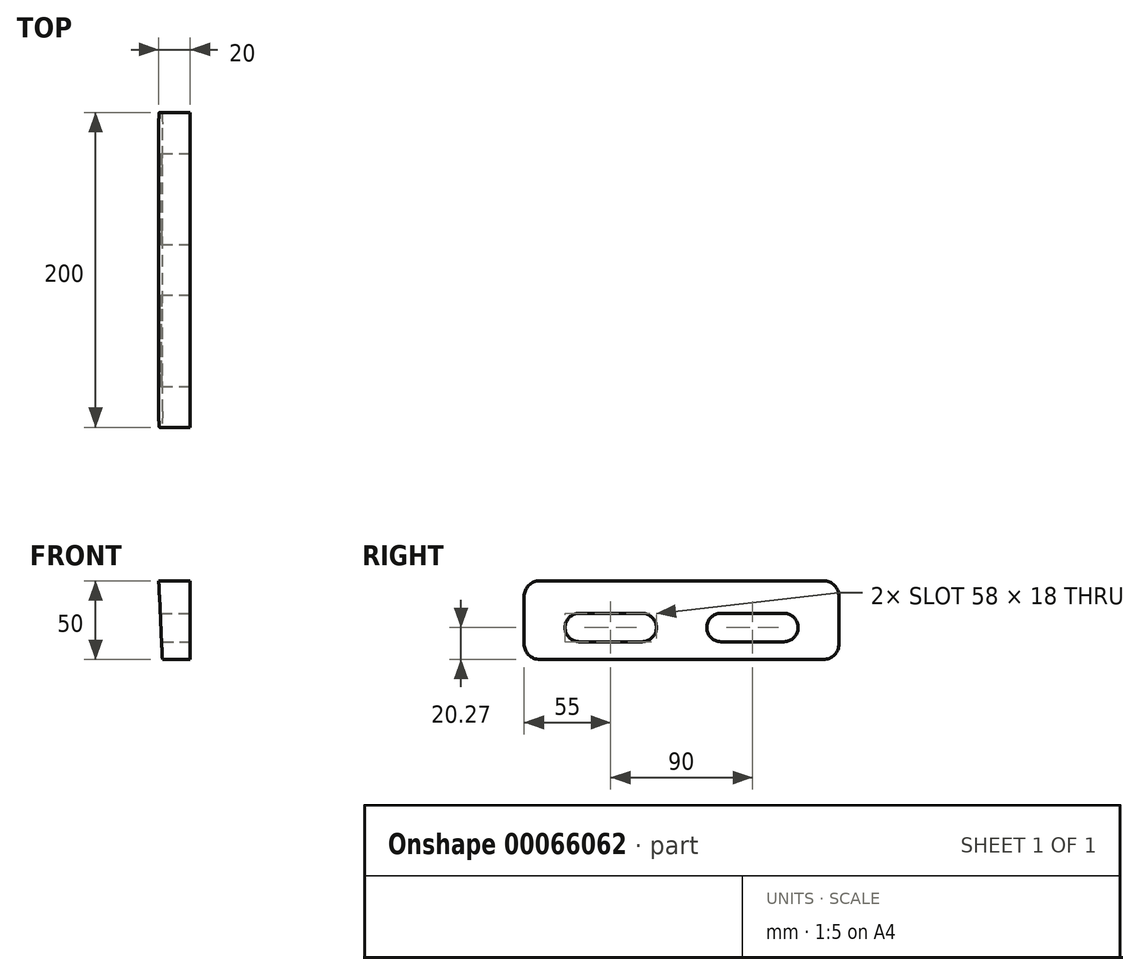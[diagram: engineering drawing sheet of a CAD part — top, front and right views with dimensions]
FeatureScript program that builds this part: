
annotation { "Feature Type Name" : "Feature", "Feature Type Description" : "" }
export const myFeature = defineFeature(function(context is Context, id is Id, definition is map)
    precondition{}
    {
        {
            var Q0;
            Q0=qCreatedBy(makeId("Front.planeOp"),FACE);
            var sketch = newSketch(context, id + "F0", { "sketchPlane" : qUnion([Q0])});
            skLineSegment(sketch, "E0", {"start": v(6.85, 29.73) * mm, "end": v(6.85, -20.27) * mm});
            skLineSegment(sketch, "E1", {"start": v(6.85, -20.27) * mm, "end": v(-10.8, -20.27) * mm});
            skLineSegment(sketch, "E2", {"start": v(-10.8, -20.27) * mm, "end": v(-13.15, 29.73) * mm});
            skLineSegment(sketch, "E3", {"start": v(-13.15, 29.73) * mm, "end": v(6.85, 29.73) * mm});
            skLineSegment(sketch, "E4", {"start": v(-13.15, 29.73) * mm, "end": v(-13.15, -60.05) * mm, "construction": true});
            skSolve(sketch);
        }
        {
            var Q0;
            Q0=makeQuery(id+"F0.imprint","IMPRINT",FACE,{"disambiguationData":[TD([[makeQuery(id+"F0.imprint","IMPRINT",EDGE,{"derivedFrom":sQuery(id+"F0.wireOp",EDGE,"E0")}),-1.0]])]});
            extrude(context, id + "F1", {"entities" : qUnion([Q0]), "depth" : 200 * mm});
        }
        {
            var Q0;
            Q0=makeQuery(id+"F1.opExtrude","SWEPT_FACE",FACE,{"disambiguationData":[OSD([sQuery(id+"F0.wireOp",EDGE,"E0")])]});
            var sketch = newSketch(context, id + "F2", { "sketchPlane" : qUnion([Q0])});
            skArc(sketch, "E5", {"start": v(-165, 9) * mm, "mid": v(-174, 0) * mm, "end": v(-165, -9) * mm});
            skArc(sketch, "E6", {"start": v(-125, -9) * mm, "mid": v(-116, 0) * mm, "end": v(-125, 9) * mm});
            skArc(sketch, "E7", {"start": v(-75, 9) * mm, "mid": v(-84, 0) * mm, "end": v(-75, -9) * mm});
            skArc(sketch, "E8", {"start": v(-35, -9) * mm, "mid": v(-26, 0) * mm, "end": v(-35, 9) * mm});
            skLineSegment(sketch, "E9", {"start": v(-165, 9) * mm, "end": v(-125, 9) * mm});
            skLineSegment(sketch, "E10", {"start": v(-125, -9) * mm, "end": v(-165, -9) * mm});
            skLineSegment(sketch, "E11", {"start": v(-35, 9) * mm, "end": v(-75, 9) * mm});
            skLineSegment(sketch, "E12", {"start": v(-35, -9) * mm, "end": v(-75, -9) * mm});
            skSolve(sketch);
        }
        {
            var Q0;
            Q0=makeQuery(id+"F2.imprint","IMPRINT",FACE,{"disambiguationData":[TD([[makeQuery(id+"F2.imprint","IMPRINT",EDGE,{"derivedFrom":sQuery(id+"F2.wireOp",EDGE,"E5")}),1.0]])]});
            var Q1;
            Q1=makeQuery(id+"F2.imprint","IMPRINT",FACE,{"disambiguationData":[TD([[makeQuery(id+"F2.imprint","IMPRINT",EDGE,{"derivedFrom":sQuery(id+"F2.wireOp",EDGE,"E7")}),1.0]])]});
            extrude(context, id + "F3", {"entities" : qUnion([Q0, Q1]), "operationType" : NewBodyOperationType.REMOVE, "endBound" : BoundingType.THROUGH_ALL, "oppositeDirection" : true, "depth" : 25 * mm});
        }
        {
            var Q0;
            Q0=makeQuery(id+"F1.opExtrude","CAP_EDGE",EDGE,{"disambiguationData":[OSD([sQuery(id+"F0.wireOp",EDGE,"E3")])],"isStart":false});
            var Q1;
            Q1=makeQuery(id+"F1.opExtrude","CAP_EDGE",EDGE,{"disambiguationData":[OSD([sQuery(id+"F0.wireOp",EDGE,"E1")])],"isStart":false});
            var Q2;
            Q2=makeQuery(id+"F1.opExtrude","CAP_EDGE",EDGE,{"disambiguationData":[OSD([sQuery(id+"F0.wireOp",EDGE,"E1")])],"isStart":true});
            var Q3;
            Q3=makeQuery(id+"F1.opExtrude","CAP_EDGE",EDGE,{"disambiguationData":[OSD([sQuery(id+"F0.wireOp",EDGE,"E3")])],"isStart":true});
            fillet(context, id + "F4", {"entities" : qUnion([Q0, Q1, Q2, Q3]), "radius" : 10 * mm, "tangentPropagation" : true, "allowEdgeOverflow" : false});
        }
    });
